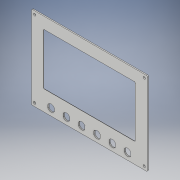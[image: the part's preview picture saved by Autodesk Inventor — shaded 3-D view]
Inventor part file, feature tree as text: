
AUTODESK INVENTOR PART (.ipt)
format: ipt  version: 2019 (Build 230136000, 136)  size: 199,168 bytes
history: native  units: in
note: dims shown in document units (in); Inventor stores cm internally (conversion verified against a paired STEP export)
features: direct_edit x2, move_body x2, extrude x1, sketch x1, imported_body x1
ambient origin geometry x8: Origin, YZ Plane, XZ Plane, XY Plane, X Axis, Y Axis, Z Axis, Center Point
bodies: Solid1 (feature_tree)
feature tree (7):
  direct_edit  "Direct Edit1"
  direct_edit  "Direct Edit2"
  extrude  "Extrusion1"  TaperAngle=0.0deg  [1 undecoded]
  sketch  "Sketch1"  dims[d0=0.0in d1=0.0in d2=0.3937in d3=0.0in d4=-0.3937in d5=0.0in d6=0.4291in d7=0.2382in d8=0.2382in d9=2.3622in d11=1.0171in d12=0.3937in d14=0.3937in d16=0.5085in d17=0.5085in d18=6.1024in d19=0.3937in d20=0.0in d21=0.8661in]
  imported_body  "Base1"
  move_body  "Move1"
  move_body  "Move2"
note: 1 required parameter value undecoded (feature->parameter linkage not recoverable at this tier; creation-order binding heuristic only, values carry confidence <= 0.55)
